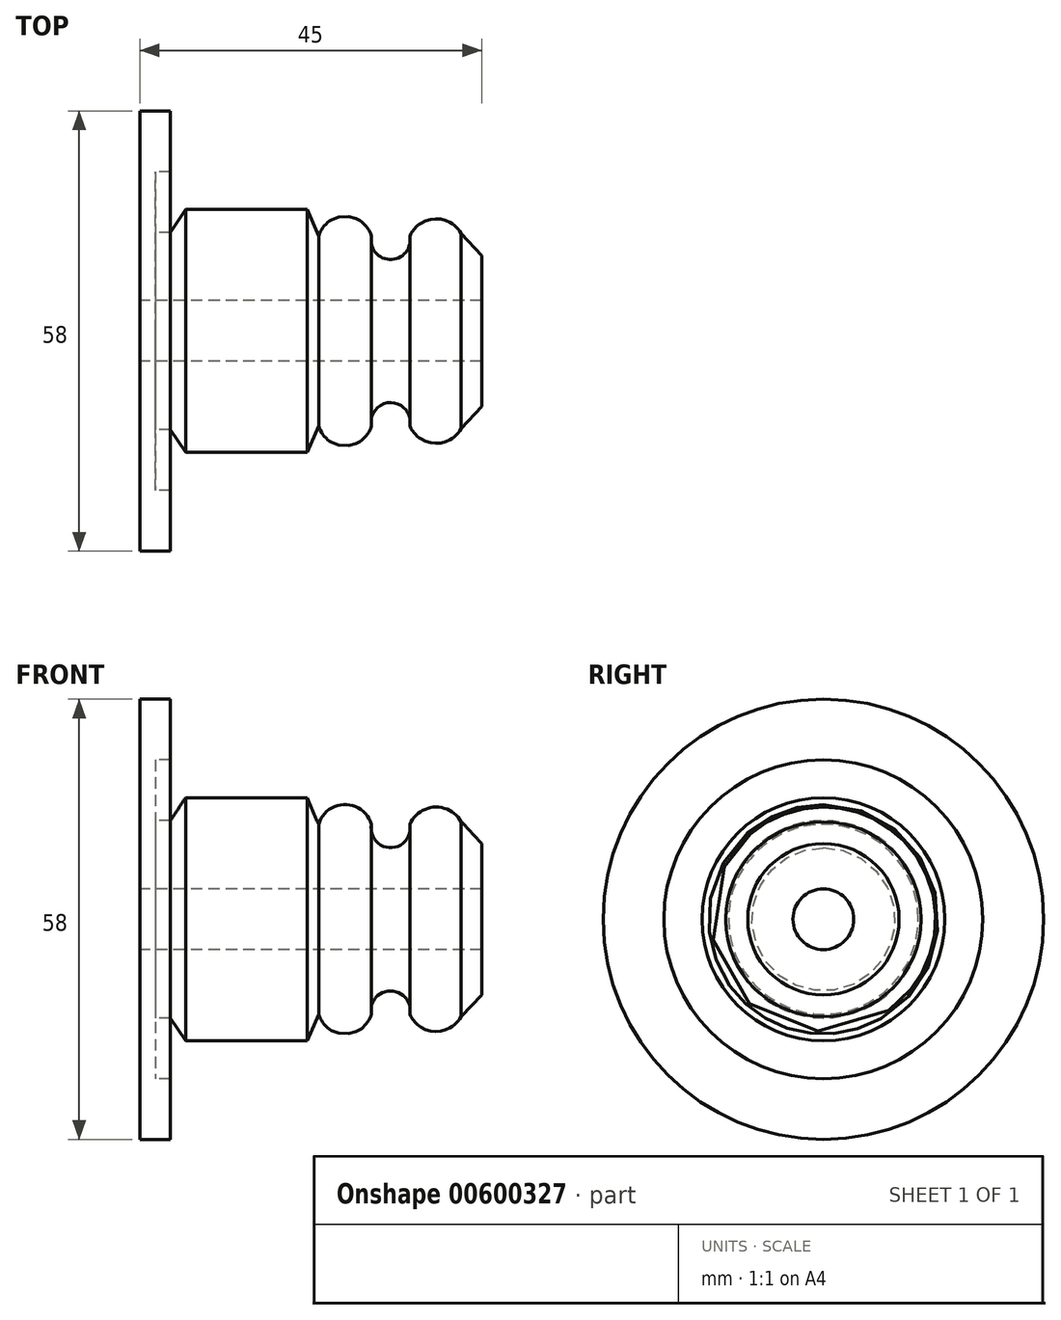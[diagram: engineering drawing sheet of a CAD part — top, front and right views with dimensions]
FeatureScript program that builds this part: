
annotation { "Feature Type Name" : "Feature", "Feature Type Description" : "" }
export const myFeature = defineFeature(function(context is Context, id is Id, definition is map)
    precondition{}
    {
        {
            var Q0;
            Q0=qCreatedBy(makeId("Front.planeOp"),FACE);
            var sketch = newSketch(context, id + "F0", { "sketchPlane" : qUnion([Q0])});
            skLineSegment(sketch, "E0", {"start": v(0, 4) * mm, "end": v(45, 4) * mm});
            skLineSegment(sketch, "E1", {"start": v(0, 4) * mm, "end": v(0, 29) * mm});
            skLineSegment(sketch, "E2", {"start": v(4, 29) * mm, "end": v(0, 29) * mm});
            skLineSegment(sketch, "E3", {"start": v(0, 0) * mm, "end": v(242.98, 0) * mm, "construction": true});
            skLineSegment(sketch, "E4", {"start": v(4, 29) * mm, "end": v(4, 21) * mm});
            skLineSegment(sketch, "E5", {"start": v(4, 21) * mm, "end": v(2, 21) * mm});
            skLineSegment(sketch, "E6", {"start": v(2, 21) * mm, "end": v(2, 13) * mm});
            skArc(sketch, "E7", {"start": v(23.53, 12.5) * mm, "mid": v(27, 15.12) * mm, "end": v(30.47, 12.5) * mm});
            skArc(sketch, "E8", {"start": v(30.47, 12.5) * mm, "mid": v(33, 9.43) * mm, "end": v(35.53, 12.5) * mm});
            skArc(sketch, "E9", {"start": v(35.53, 12.5) * mm, "mid": v(38.8, 14.78) * mm, "end": v(42.3, 12.85) * mm});
            skLineSegment(sketch, "E10", {"start": v(6, 16) * mm, "end": v(22, 16) * mm});
            skLineSegment(sketch, "E11", {"start": v(22, 16) * mm, "end": v(23.53, 12.5) * mm});
            skLineSegment(sketch, "E12", {"start": v(45, 4) * mm, "end": v(45, 9.97) * mm});
            skLineSegment(sketch, "E13", {"start": v(45, 9.97) * mm, "end": v(42.3, 12.85) * mm});
            skLineSegment(sketch, "E14", {"start": v(2, 13) * mm, "end": v(4, 13) * mm});
            skLineSegment(sketch, "E15", {"start": v(4, 13) * mm, "end": v(6, 16) * mm});
            skSolve(sketch);
        }
        {
            var Q0;
            Q0=qCreatedBy(makeId("Front.planeOp"),FACE);
            var sketch = newSketch(context, id + "F1", { "sketchPlane" : qUnion([Q0])});
            skLineSegment(sketch, "E16", {"start": v(-76.18, 0) * mm, "end": v(171.45, 0) * mm, "construction": true});
            skSolve(sketch);
        }
        {
            var Q0;
            Q0 = qSketchRegion(id + "F0", true);
            var Q1;
            Q1=sQuery(id+"F1.wireOp",EDGE,"E16");
            revolve(context, id + "F2", {"entities" : qUnion([Q0]), "axis" : qUnion([Q1]), "revolveType" : RevolveType.FULL});
        }
    });
